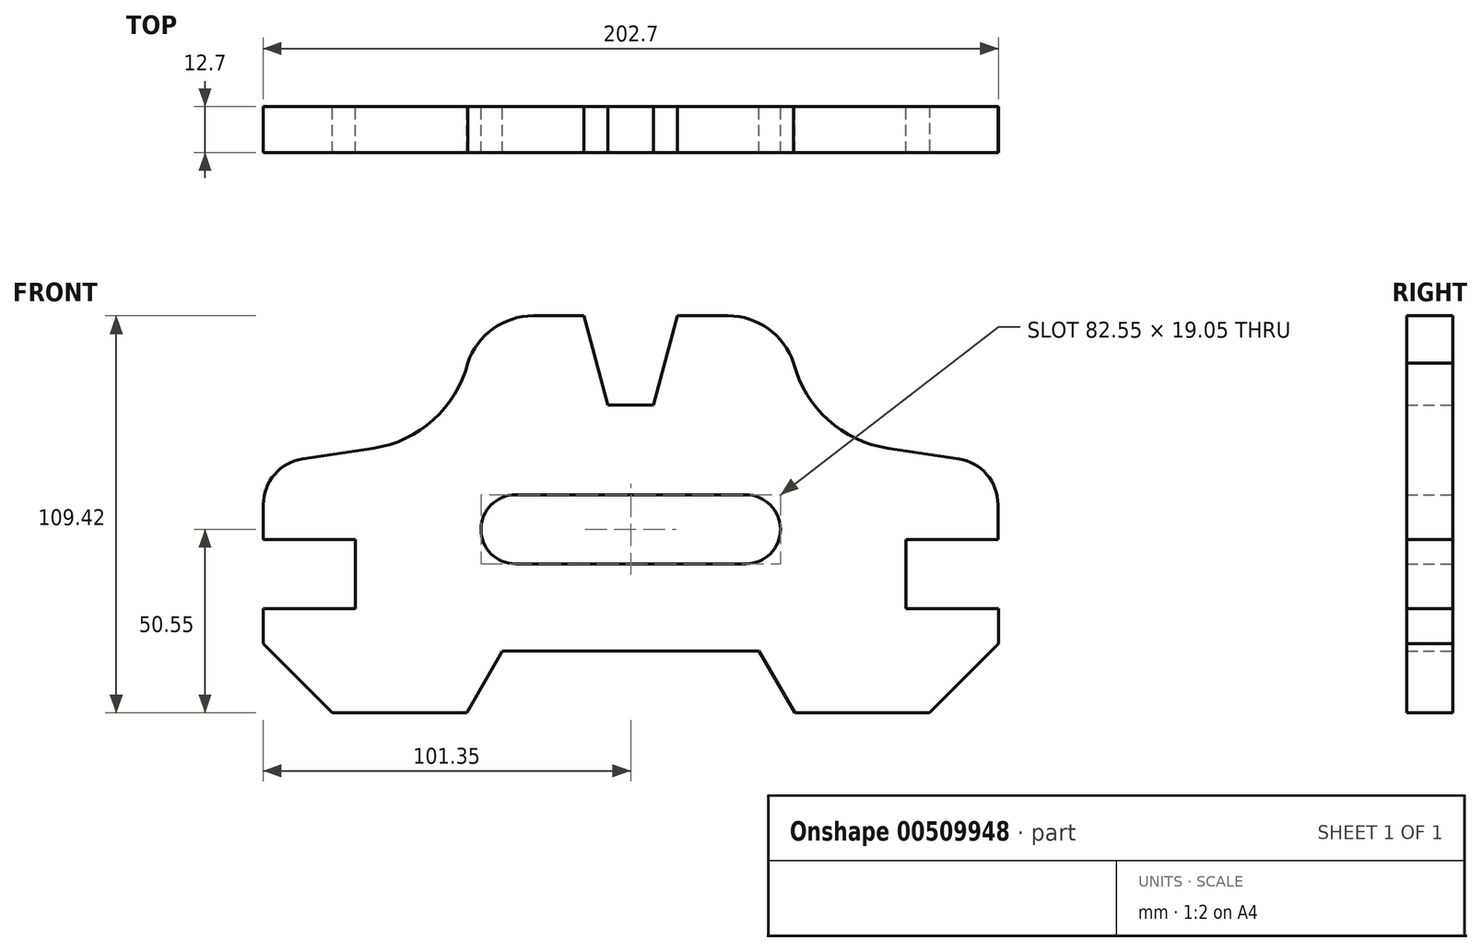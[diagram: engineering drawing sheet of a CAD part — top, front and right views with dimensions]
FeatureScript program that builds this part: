
annotation { "Feature Type Name" : "Feature", "Feature Type Description" : "" }
export const myFeature = defineFeature(function(context is Context, id is Id, definition is map)
    precondition{}
    {
        {
            var Q0;
            Q0=qCreatedBy(makeId("Front.planeOp"),FACE);
            var sketch = newSketch(context, id + "F0", { "sketchPlane" : qUnion([Q0])});
            skLineSegment(sketch, "E0", {"start": v(75.84, -21.84) * mm, "end": v(75.84, -2.8) * mm});
            skLineSegment(sketch, "E1", {"start": v(75.84, -21.84) * mm, "end": v(101.35, -21.84) * mm});
            skLineSegment(sketch, "E2", {"start": v(101.35, -21.84) * mm, "end": v(101.35, -50.55) * mm});
            skArc(sketch, "E3", {"start": v(70.95, 22.35) * mm, "mid": v(54.4, 30.18) * mm, "end": v(44.92, 45.86) * mm});
            skLineSegment(sketch, "E4", {"start": v(101.35, -50.55) * mm, "end": v(45.21, -50.55) * mm});
            skLineSegment(sketch, "E5", {"start": v(45.21, -50.55) * mm, "end": v(35.42, -33.55) * mm});
            skLineSegment(sketch, "E6.bottom", {"start": v(31.75, 9.53) * mm, "end": v(-31.75, 9.53) * mm});
            skLineSegment(sketch, "E6.top", {"start": v(31.75, -9.52) * mm, "end": v(-31.75, -9.52) * mm});
            skPoint(sketch, "E6.middle", {"position": v(0, 0) * mm});
            skLineSegment(sketch, "E7", {"start": v(70.95, 22.35) * mm, "end": v(90.43, 19.42) * mm});
            skArc(sketch, "E8", {"start": v(90.43, 19.42) * mm, "mid": v(98.17, 15.14) * mm, "end": v(101.24, 6.86) * mm});
            skPoint(sketch, "E9.endSnap0", {"position": v(0, 9.53) * mm});
            skLineSegment(sketch, "E10.MirrorCS", {"start": v(-70.95, 22.35) * mm, "end": v(-90.43, 19.42) * mm});
            skArc(sketch, "E11.MirrorCS", {"start": v(-90.43, 19.42) * mm, "mid": v(-98.17, 15.14) * mm, "end": v(-101.24, 6.86) * mm});
            skLineSegment(sketch, "E12.MirrorCS", {"start": v(-75.84, -21.84) * mm, "end": v(-101.35, -21.84) * mm});
            skLineSegment(sketch, "E13.MirrorCS", {"start": v(-101.35, -21.84) * mm, "end": v(-101.35, -50.55) * mm});
            skLineSegment(sketch, "E14.MirrorCS", {"start": v(-101.35, -50.55) * mm, "end": v(-45.21, -50.55) * mm});
            skLineSegment(sketch, "E15.MirrorCS", {"start": v(-45.21, -50.55) * mm, "end": v(-35.42, -33.55) * mm});
            skLineSegment(sketch, "E16", {"start": v(-35.42, -33.55) * mm, "end": v(0, -33.55) * mm});
            skLineSegment(sketch, "E17", {"start": v(0, -33.55) * mm, "end": v(35.42, -33.55) * mm});
            skLineSegment(sketch, "E18", {"start": v(-101.24, -2.8) * mm, "end": v(-101.24, 6.86) * mm});
            skLineSegment(sketch, "E19", {"start": v(101.24, 6.86) * mm, "end": v(101.24, -2.8) * mm});
            skLineSegment(sketch, "E20", {"start": v(101.24, -2.8) * mm, "end": v(75.84, -2.8) * mm});
            skLineSegment(sketch, "E21", {"start": v(-6.45, 34.23) * mm, "end": v(6.25, 34.23) * mm});
            skLineSegment(sketch, "E22", {"start": v(6.25, 34.23) * mm, "end": v(12.85, 58.87) * mm});
            skLineSegment(sketch, "E23.MirrorCS", {"start": v(-6.25, 34.23) * mm, "end": v(-12.85, 58.87) * mm});
            skLineSegment(sketch, "E24", {"start": v(-101.24, -2.8) * mm, "end": v(-75.84, -2.8) * mm});
            skLineSegment(sketch, "E25", {"start": v(-75.84, -2.8) * mm, "end": v(-75.84, -21.84) * mm});
            skLineSegment(sketch, "E26", {"start": v(-12.85, 58.87) * mm, "end": v(-26.85, 58.87) * mm});
            skArc(sketch, "E27", {"start": v(-70.95, 22.35) * mm, "mid": v(-54.4, 30.18) * mm, "end": v(-44.92, 45.86) * mm});
            skArc(sketch, "E28", {"start": v(-26.85, 58.87) * mm, "mid": v(-37.98, 55.28) * mm, "end": v(-44.92, 45.86) * mm});
            skArc(sketch, "E29.MirrorCS", {"start": v(26.85, 58.87) * mm, "mid": v(37.98, 55.28) * mm, "end": v(44.92, 45.86) * mm});
            skLineSegment(sketch, "E30.MirrorCS", {"start": v(12.85, 58.87) * mm, "end": v(26.85, 58.87) * mm});
            skArc(sketch, "E31", {"start": v(-31.75, 9.53) * mm, "mid": v(-41.28, 0) * mm, "end": v(-31.75, -9.52) * mm});
            skArc(sketch, "E32", {"start": v(31.75, -9.52) * mm, "mid": v(41.28, 0) * mm, "end": v(31.75, 9.53) * mm});
            skSolve(sketch);
        }
        {
            var Q0;
            Q0 = qSketchRegion(id + "F0", true);
            extrude(context, id + "F1", {"entities" : qUnion([Q0]), "endBound" : BoundingType.SYMMETRIC, "depth" : 12.7 * mm});
        }
        {
            var Q0;
            Q0=makeQuery(id+"F1.opExtrude","SWEPT_EDGE",EDGE,{"disambiguationData":[OSD([sQuery(id+"F0.wireOp",EDGE,"E2"),sQuery(id+"F0.wireOp",EDGE,"E4")])]});
            chamfer(context, id + "F2", {"entities" : qUnion([Q0]), "chamferType" : ChamferType.OFFSET_ANGLE, "width" : 19.05 * mm, "oppositeDirection" : false, "angle" : 45 * degree, "tangentPropagation" : true});
        }
        {
            var Q0;
            Q0=makeQuery(id+"F1.opExtrude","SWEPT_EDGE",EDGE,{"disambiguationData":[OSD([sQuery(id+"F0.wireOp",EDGE,"E13.MirrorCS"),sQuery(id+"F0.wireOp",EDGE,"E14.MirrorCS")])]});
            chamfer(context, id + "F3", {"entities" : qUnion([Q0]), "chamferType" : ChamferType.OFFSET_ANGLE, "width" : 19.05 * mm, "oppositeDirection" : false, "angle" : 45 * degree, "tangentPropagation" : true});
        }
    });
